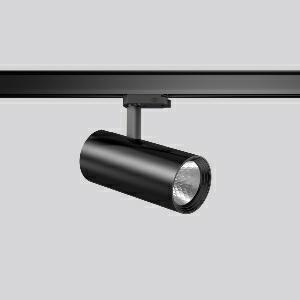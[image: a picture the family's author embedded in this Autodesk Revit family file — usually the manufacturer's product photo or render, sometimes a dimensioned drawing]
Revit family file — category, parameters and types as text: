
# Revit family: deecos_s_mini_742193_003_b58b
name_source: partatom
category: Lighting Fixtures
units: mm (PartAtom-declared; Revit-internal decimal feet)

## family parameters
Cut with Voids When Loaded = No
Host = Face
Light Source = No
Part Type = Normal
Room Calculation Point = No
Round Connector Dimension = Use Diameter
Shared = No

## types (1)
- DEECOS S mini (1 x LED Modul 930, 2200 lm, 3000)
    Apparent Load = 22 VA
    Approval mark = CE
    CIE Flux Codes = 100 100 100 100 100
    Color Rendering = 90
    Color Temperature = 3000
    Default Elevation = 1800 mm
    Description = Series: DEECOS S mini
LED surface-mounted projector in modern design with no visible cooling ribs. Housing: die-cast aluminium, powder-coated. Rotation range: 356°. Swivel range: 90°. Black plastic ring and recessed LED to prevent glare from the side. Optical assembly with reflector made of MIRO-Silver with 98% total light reflection for outstanding efficiency - can be changed without tools. Best colour rendering index Ra>90. Superspot version with small spot LED. With multi adaptor for 3-circuit tracks 230 V. Suitable for Track on ceiling, Wall track. High quality converter without flickering and stroboscopic effect. The following accessories can be mounted without use of tools: interchangeable lenses, decorative glasses, honeycomb louvre, clear and frosted diffusers, white interchangeable plastic ring. 
Colour: deep black, matt (RAL 9005)
Diameter: 87 mm
Height: 214 mm
Lamp: LED
Socket: without socket
Colour temperature: 3000K
Colour rendering index (CRI): 92
System power: 22 W
Rated luminous flux: 2200 lm
Luminous efficiency: 100 lm/W
Control gear: Regulated power supply
Protection class: I
Type of protection: IP 20
    Height = 214 mm
    Lamp = 1 x LED Modul 930
    Lamp Light Flux = 2200 lm
    Lamp count = 1
    Length = 87 mm
    Lifetime = 50000 h
    Luminous efficacy = 100 lm/W
    Manufacturer = RZB
    ModVariant = No
    Model = 742193.003
    Mounting Place = Ceiling
    Mounting Type = Rail mounted
    Number of Poles = 1
    OnlyDefault = Yes
    Power Factor = 1
    Product Name = DEECOS S mini
    Product group = Track mounted projectors
    ProductGroupID = 301
    Protection Class = Protection class I
    Protection Degree = IP 20
    RLX_Detail_Level = 1
    RLX_Emergency_Light_Flux = 0 lm
    RLX_Emergency_Type = 0
    RLX_Emergency_Type_DB = No
    RlxData = <blob elided: 38777 chars, md5=013cb44c>
    Socket = socket
    Standby Power = 0 W
    System Light Flux = 2200 lm
    System Power = 22 W
    Type Comments = Product without accessories
    Type Image = 741926.003.jpg
    URL = http://relux.com
    VarID = ---
    Voltage = 230 V
    Voltage Range = 220-240 V
    Weight = 0.00 kg
    Width = 0 mm  [stored 0 ft]

note: [stored X ft] marks values corroborated as IEEE doubles in the binary element streams (Revit-internal decimal feet)

## geometry (parser evidence)
native form markers: Blend x4, Sweep x11
no freeform markers — native parametric forms only
